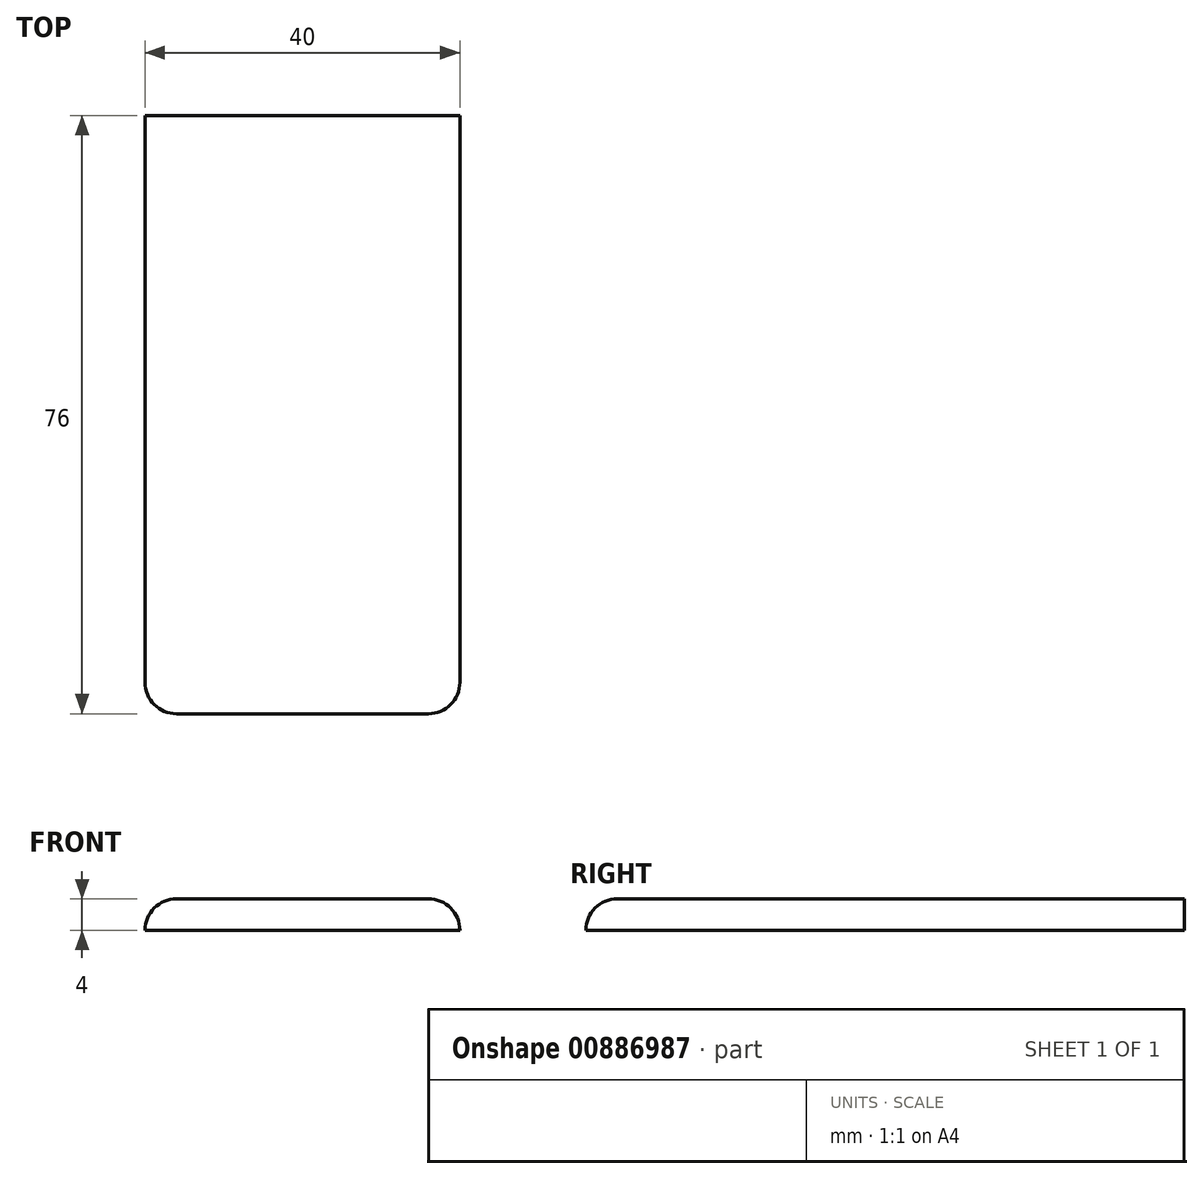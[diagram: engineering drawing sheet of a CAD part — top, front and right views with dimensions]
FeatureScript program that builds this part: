
annotation { "Feature Type Name" : "Feature", "Feature Type Description" : "" }
export const myFeature = defineFeature(function(context is Context, id is Id, definition is map)
    precondition{}
    {
        {
            var Q0;
            Q0=qCreatedBy(makeId("Top.planeOp"),FACE);
            var sketch = newSketch(context, id + "F0", { "sketchPlane" : qUnion([Q0])});
            skLineSegment(sketch, "E0.bottom", {"start": v(0, 0) * mm, "end": v(40, 0) * mm});
            skLineSegment(sketch, "E0.top", {"start": v(0, 76) * mm, "end": v(40, 76) * mm});
            skLineSegment(sketch, "E0.left", {"start": v(0, 0) * mm, "end": v(0, 76) * mm});
            skLineSegment(sketch, "E0.right", {"start": v(40, 0) * mm, "end": v(40, 76) * mm});
            skSolve(sketch);
        }
        {
            var Q0;
            Q0 = qSketchRegion(id + "F0", true);
            extrude(context, id + "F1", {"entities" : qUnion([Q0]), "depth" : 4 * mm, "offsetDistance" : 25 * mm});
        }
        {
            var Q0;
            Q0=makeQuery(id+"F1.opExtrude","CAP_EDGE",EDGE,{"disambiguationData":[OSD([sQuery(id+"F0.wireOp",EDGE,"E0.right")])],"isStart":false});
            var Q1;
            Q1=makeQuery(id+"F1.opExtrude","CAP_EDGE",EDGE,{"disambiguationData":[OSD([sQuery(id+"F0.wireOp",EDGE,"E0.bottom")])],"isStart":false});
            var Q2;
            Q2=makeQuery(id+"F1.opExtrude","CAP_EDGE",EDGE,{"disambiguationData":[OSD([sQuery(id+"F0.wireOp",EDGE,"E0.left")])],"isStart":false});
            var Q3;
            Q3=makeQuery(id+"F1.opExtrude","SWEPT_EDGE",EDGE,{"disambiguationData":[OSD([sQuery(id+"F0.wireOp",EDGE,"E0.bottom"),sQuery(id+"F0.wireOp",EDGE,"E0.right")])]});
            var Q4;
            Q4=makeQuery(id+"F1.opExtrude","SWEPT_EDGE",EDGE,{"disambiguationData":[OSD([sQuery(id+"F0.wireOp",EDGE,"E0.bottom"),sQuery(id+"F0.wireOp",EDGE,"E0.left")])]});
            fillet(context, id + "F2", {"entities" : qUnion([Q0, Q1, Q2, Q3, Q4]), "radius" : 4 * mm, "tangentPropagation" : true, "allowEdgeOverflow" : false});
        }
    });
